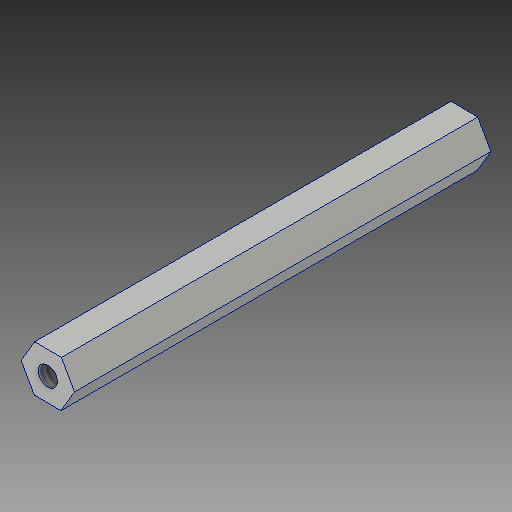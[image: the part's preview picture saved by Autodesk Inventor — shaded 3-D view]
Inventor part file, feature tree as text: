
AUTODESK INVENTOR PART (.ipt)
format: ipt  version: 2019 (Build 230136000, 136)  size: 101,376 bytes
history: native  units: in
note: dims shown in document units (in); Inventor stores cm internally (conversion verified against a paired STEP export)
features: sketch x1, extrude x1, hole x1
ambient origin geometry x8: Origin, YZ Plane, XZ Plane, XY Plane, X Axis, Y Axis, Z Axis, Center Point
bodies: Solid1 (feature_tree)
feature tree (3):
  sketch  "Sketch1"  dims[d0=0.25in d1=2.25in d2=0.0in d3=0.104in d4=2.25in d5=0.375in d6=0.25in d7=0.5635in d8=2.25in d9=0.8108in]
  extrude  "Extrusion1"  Depth=2.25in TaperAngle=0.0deg
  hole  "Hole1"  [1 undecoded]
note: 1 required parameter value undecoded (feature->parameter linkage not recoverable at this tier; creation-order binding heuristic only, values carry confidence <= 0.55)
